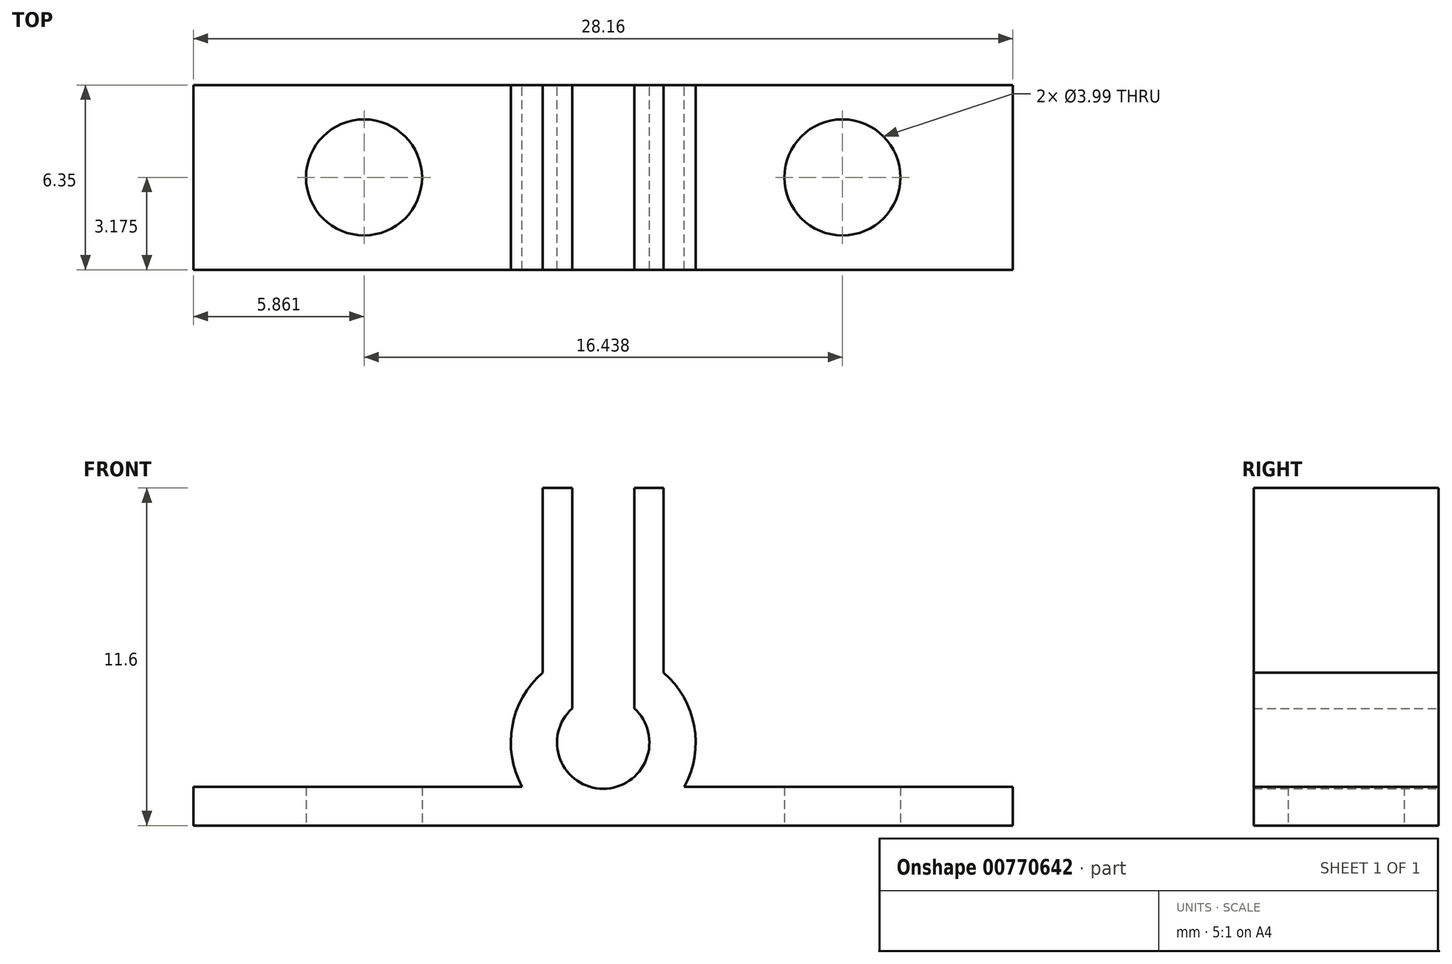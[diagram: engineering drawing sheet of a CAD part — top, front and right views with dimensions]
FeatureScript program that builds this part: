
annotation { "Feature Type Name" : "Feature", "Feature Type Description" : "" }
export const myFeature = defineFeature(function(context is Context, id is Id, definition is map)
    precondition{}
    {
        {
            var Q0;
            Q0=qCreatedBy(makeId("Front.planeOp"),FACE);
            var sketch = newSketch(context, id + "F0", { "sketchPlane" : qUnion([Q0])});
            skArc(sketch, "E0", {"start": v(-1.07, 1.18) * mm, "mid": v(0, -1.59) * mm, "end": v(1.07, 1.18) * mm});
            skLineSegment(sketch, "E1.left", {"start": v(-2.08, 4.2) * mm, "end": v(-2.08, 2.4) * mm});
            skLineSegment(sketch, "E1.right", {"start": v(-1.07, 4.2) * mm, "end": v(-1.07, 1.18) * mm});
            skLineSegment(sketch, "E2.MirrorCS", {"start": v(1.07, 4.2) * mm, "end": v(1.07, 1.18) * mm});
            skLineSegment(sketch, "E3.MirrorCS", {"start": v(2.08, 4.2) * mm, "end": v(2.08, 2.4) * mm});
            skPoint(sketch, "E4.orphan", {"position": v(-2.08, 0.57) * mm});
            skPoint(sketch, "E5.orphan", {"position": v(2.08, 0.57) * mm});
            skPoint(sketch, "E6.orphan", {"position": v(1.07, 0.57) * mm});
            skPoint(sketch, "E1.top.end.orphan", {"position": v(-1.07, 0.57) * mm});
            skLineSegment(sketch, "E7.left", {"start": v(-1.38, -1.52) * mm, "end": v(-1.38, -15.5) * mm, "construction": true});
            skLineSegment(sketch, "E7.right", {"start": v(-1.4, -2.85) * mm, "end": v(-1.4, -15.5) * mm, "construction": true});
            skLineSegment(sketch, "E8.MirrorCS", {"start": v(1.4, -2.85) * mm, "end": v(1.4, -15.5) * mm, "construction": true});
            skLineSegment(sketch, "E9.MirrorCS", {"start": v(1.38, -1.52) * mm, "end": v(1.38, -15.5) * mm, "construction": true});
            skPoint(sketch, "E10.orphan", {"position": v(-1.4, -1.52) * mm});
            skPoint(sketch, "E11.MirrorCS.end.orphan", {"position": v(1.4, -1.52) * mm});
            skPoint(sketch, "E11.MirrorCS.start.orphan", {"position": v(1.38, -1.52) * mm});
            skLineSegment(sketch, "E12", {"start": v(-2.08, 4.2) * mm, "end": v(-2.08, 8.75) * mm});
            skLineSegment(sketch, "E13", {"start": v(-1.07, 8.75) * mm, "end": v(-1.07, 4.2) * mm});
            skLineSegment(sketch, "E14.MirrorCS", {"start": v(1.07, 8.75) * mm, "end": v(1.07, 4.2) * mm});
            skLineSegment(sketch, "E15.MirrorCS", {"start": v(2.08, 4.2) * mm, "end": v(2.08, 8.75) * mm});
            skPoint(sketch, "E16.MirrorCS.end.orphan", {"position": v(1.07, 4.2) * mm});
            skPoint(sketch, "E16.MirrorCS.start.orphan", {"position": v(2.08, 4.2) * mm});
            skPoint(sketch, "E17.MirrorCS.end.orphan", {"position": v(1.4, -15.5) * mm});
            skPoint(sketch, "E17.MirrorCS.start.orphan", {"position": v(1.38, -15.5) * mm});
            skArc(sketch, "E18", {"start": v(1.38, -2.86) * mm, "mid": v(0, 3.18) * mm, "end": v(-1.38, -2.86) * mm});
            skLineSegment(sketch, "E19", {"start": v(-1.07, 4.2) * mm, "end": v(-1.07, 3) * mm, "construction": true});
            skLineSegment(sketch, "E20", {"start": v(1.07, 4.2) * mm, "end": v(1.07, 3) * mm});
            skLineSegment(sketch, "E21", {"start": v(-1.38, -1.52) * mm, "end": v(-14.08, -1.52) * mm});
            skLineSegment(sketch, "E22", {"start": v(-1.4, -2.85) * mm, "end": v(-14.08, -2.85) * mm});
            skLineSegment(sketch, "E23", {"start": v(-14.08, -2.85) * mm, "end": v(-14.08, -1.52) * mm});
            skLineSegment(sketch, "E24", {"start": v(1.38, -1.52) * mm, "end": v(14.08, -1.52) * mm});
            skLineSegment(sketch, "E25", {"start": v(14.08, -1.52) * mm, "end": v(14.08, -2.85) * mm});
            skLineSegment(sketch, "E26", {"start": v(14.08, -2.85) * mm, "end": v(1.4, -2.85) * mm});
            skLineSegment(sketch, "E27", {"start": v(-1.4, -2.85) * mm, "end": v(1.4, -2.85) * mm});
            skLineSegment(sketch, "E28", {"start": v(1.07, 8.75) * mm, "end": v(2.08, 8.75) * mm});
            skPoint(sketch, "E29.MirrorCS.end.orphan", {"position": v(1.07, 10.98) * mm});
            skPoint(sketch, "E29.MirrorCS.start.orphan", {"position": v(2.08, 10.98) * mm});
            skLineSegment(sketch, "E30.MirrorCS", {"start": v(-1.07, 8.75) * mm, "end": v(-2.08, 8.75) * mm});
            skPoint(sketch, "E31.start.orphan", {"position": v(-2.08, 10.98) * mm});
            skPoint(sketch, "E32.orphan", {"position": v(-1.07, 10.98) * mm});
            skSolve(sketch);
        }
        {
            var Q0;
            {var subQ4=sQuery(id+"F0.wireOp",EDGE,"E1.left");Q0=makeQuery(id+"F0.imprint","IMPRINT",FACE,{"disambiguationData":[TD([[makeQuery(id+"F0.imprint","IMPRINT",EDGE,{"derivedFrom":subQ4}),1.0]])]});}
            var Q1;
            {var subQ3=sQuery(id+"F0.wireOp",EDGE,"E0");Q1=makeQuery(id+"F0.imprint","IMPRINT",FACE,{"disambiguationData":[TD([[makeQuery(id+"F0.imprint","IMPRINT",EDGE,{"derivedFrom":subQ3}),-1.0]])]});}
            var Q2;
            {var subQ1=sQuery(id+"F0.wireOp",EDGE,"E3.MirrorCS");Q2=makeQuery(id+"F0.imprint","IMPRINT",FACE,{"disambiguationData":[TD([[makeQuery(id+"F0.imprint","IMPRINT",EDGE,{"derivedFrom":subQ1}),-1.0]])]});}
            var Q3;
            {var subQ4=sQuery(id+"F0.wireOp",EDGE,"E25");Q3=makeQuery(id+"F0.imprint","IMPRINT",FACE,{"disambiguationData":[TD([[makeQuery(id+"F0.imprint","IMPRINT",EDGE,{"derivedFrom":subQ4}),-1.0]])]});}
            var Q4;
            {var subQ3=sQuery(id+"F0.wireOp",EDGE,"E22");Q4=makeQuery(id+"F0.imprint","IMPRINT",FACE,{"disambiguationData":[TD([[makeQuery(id+"F0.imprint","IMPRINT",EDGE,{"derivedFrom":subQ3}),-1.0]])]});}
            extrude(context, id + "F1", {"entities" : qUnion([Q0, Q1, Q2, Q3, Q4]), "depth" : 6.35 * mm, "offsetDistance" : 25.4 * mm});
        }
        {
            var Q0;
            Q0=qCreatedBy(makeId("Top.planeOp"),FACE);
            cPlane(context, id + "F2", {"entities" : qUnion([Q0]), "cplaneType" : CPlaneType.OFFSET, "offset" : 2.03 * mm, "oppositeDirection" : true, "width" : 152.4 * mm, "height" : 152.4 * mm});
        }
        {
            var Q0;
            Q0=makeQuery(id+"F1.opExtrude","SWEPT_FACE",FACE,{"disambiguationData":[OSD([sQuery(id+"F0.wireOp",EDGE,"E22"),sQuery(id+"F0.wireOp",EDGE,"E26"),sQuery(id+"F0.wireOp",EDGE,"E27")])]});
            var sketch = newSketch(context, id + "F3", { "sketchPlane" : qUnion([Q0])});
            skCircle(sketch, "E33", {"center": v(-8.22, 3.18) * mm, "radius": 1.43 * mm});
            skCircle(sketch, "E34.MirrorC", {"center": v(8.22, 3.18) * mm, "radius": 1.43 * mm});
            skSolve(sketch);
        }
        {
            var Q0;
            Q0=sQuery(id+"F3.wireOp",VERTEX,"E33.center");
            var Q1;
            Q1=sQuery(id+"F3.wireOp",VERTEX,"E34.MirrorC.center");
            var Q2;
            Q2=makeQuery(id+"F1.opExtrude","SWEPT_BODY",BODY,{"disambiguationData":[OSD([sQuery(id+"F0.wireOp",EDGE,"E0"),sQuery(id+"F0.wireOp",EDGE,"E1.left"),sQuery(id+"F0.wireOp",EDGE,"E1.right"),sQuery(id+"F0.wireOp",EDGE,"E2.MirrorCS"),sQuery(id+"F0.wireOp",EDGE,"E3.MirrorCS"),sQuery(id+"F0.wireOp",EDGE,"E12"),sQuery(id+"F0.wireOp",EDGE,"E13"),sQuery(id+"F0.wireOp",EDGE,"E14.MirrorCS"),sQuery(id+"F0.wireOp",EDGE,"E15.MirrorCS"),sQuery(id+"F0.wireOp",EDGE,"E18"),sQuery(id+"F0.wireOp",EDGE,"E21"),sQuery(id+"F0.wireOp",EDGE,"E22"),sQuery(id+"F0.wireOp",EDGE,"E23"),sQuery(id+"F0.wireOp",EDGE,"E24"),sQuery(id+"F0.wireOp",EDGE,"E25"),sQuery(id+"F0.wireOp",EDGE,"E26"),sQuery(id+"F0.wireOp",EDGE,"E27"),sQuery(id+"F0.wireOp",EDGE,"E28"),sQuery(id+"F0.wireOp",EDGE,"E30.MirrorCS")])]});
            hole(context, id + "F4", {"style" : HoleStyle.SIMPLE, "endStyle" : HoleEndStyle.THROUGH, "holeDiameter" : 4 * mm, "majorDiameter" : 6.35 * mm, "isTappedThrough" : true, "tappedDepth" : 12.7 * mm, "tapClearance" : 3, "locations" : qUnion([Q0, Q1]), "scope" : qUnion([Q2])});
        }
    });
